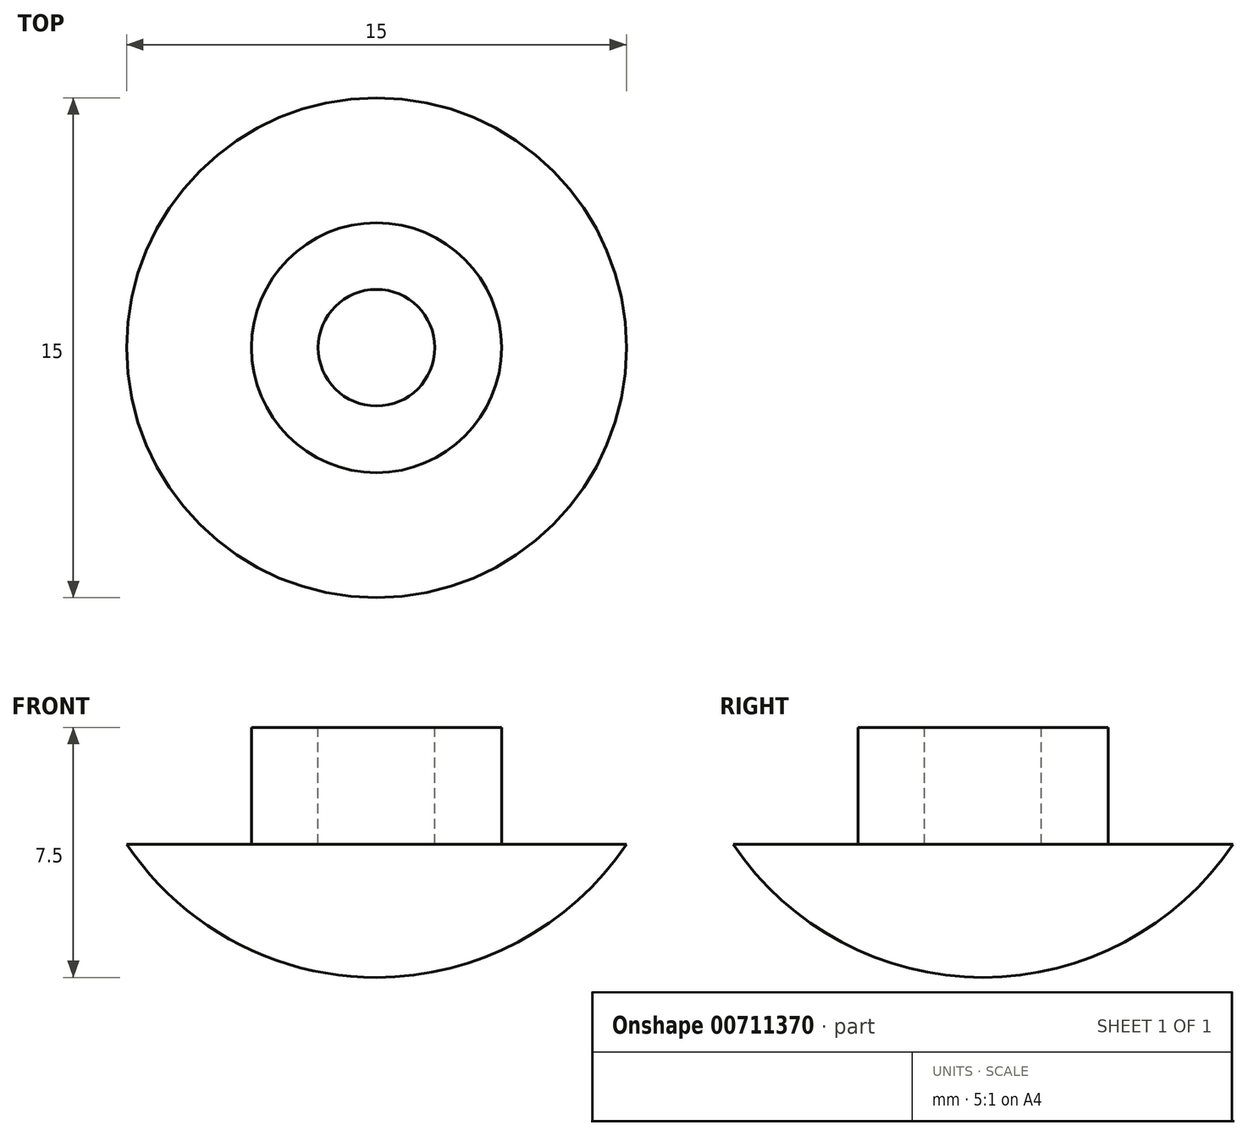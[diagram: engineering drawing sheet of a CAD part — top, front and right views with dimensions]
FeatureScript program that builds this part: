
annotation { "Feature Type Name" : "Feature", "Feature Type Description" : "" }
export const myFeature = defineFeature(function(context is Context, id is Id, definition is map)
    precondition{}
    {
        {
            var Q0;
            Q0=qCreatedBy(makeId("Front.planeOp"),FACE);
            var sketch = newSketch(context, id + "F0", { "sketchPlane" : qUnion([Q0])});
            skLineSegment(sketch, "E0", {"start": v(3.75, 7.5) * mm, "end": v(3.75, 4) * mm});
            skLineSegment(sketch, "E1", {"start": v(3.75, 4) * mm, "end": v(7.5, 4) * mm});
            skLineSegment(sketch, "E2", {"start": v(3.75, 7.5) * mm, "end": v(1.75, 7.5) * mm});
            skLineSegment(sketch, "E3", {"start": v(1.75, 7.5) * mm, "end": v(1.75, 4) * mm});
            skLineSegment(sketch, "E4", {"start": v(1.75, 4) * mm, "end": v(0, 4) * mm});
            skLineSegment(sketch, "E5", {"start": v(0, 4) * mm, "end": v(0, 0) * mm});
            skArc(sketch, "E6", {"start": v(0, 0) * mm, "mid": v(4.25, 1.06) * mm, "end": v(7.5, 4) * mm});
            skLineSegment(sketch, "E7", {"start": v(3.75, 4) * mm, "end": v(1.75, 4) * mm, "construction": true});
            skSolve(sketch);
        }
        {
            var Q0;
            Q0 = qSketchRegion(id + "F0", true);
            var Q1;
            Q1=sQuery(id+"F0.wireOp",EDGE,"E5");
            revolve(context, id + "F1", {"surfaceOperationType" : NewSurfaceOperationType.NEW, "entities" : qUnion([Q0]), "axis" : qUnion([Q1]), "revolveType" : RevolveType.FULL});
        }
    });
